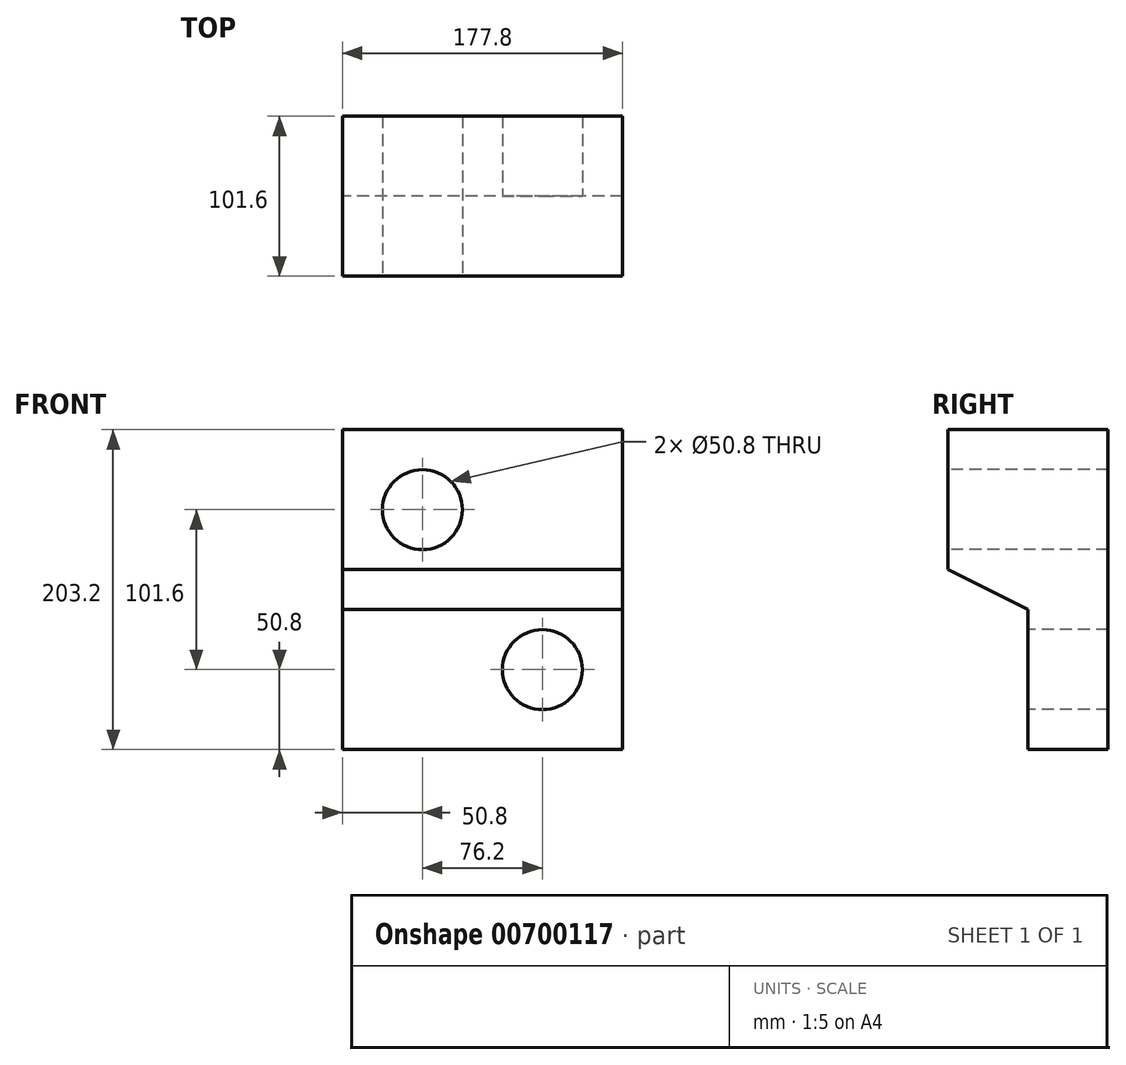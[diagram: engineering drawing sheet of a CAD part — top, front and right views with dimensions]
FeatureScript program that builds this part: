
annotation { "Feature Type Name" : "Feature", "Feature Type Description" : "" }
export const myFeature = defineFeature(function(context is Context, id is Id, definition is map)
    precondition{}
    {
        {
            var Q0;
            Q0=qCreatedBy(makeId("Right.planeOp"),FACE);
            var sketch = newSketch(context, id + "F0", { "sketchPlane" : qUnion([Q0])});
            skLineSegment(sketch, "E0", {"start": v(0, -88.9) * mm, "end": v(0, 0) * mm});
            skLineSegment(sketch, "E1", {"start": v(0, -88.9) * mm, "end": v(50.8, -88.9) * mm});
            skLineSegment(sketch, "E2", {"start": v(50.8, -88.9) * mm, "end": v(50.8, 114.3) * mm});
            skLineSegment(sketch, "E3", {"start": v(50.8, 114.3) * mm, "end": v(-50.8, 114.3) * mm});
            skLineSegment(sketch, "E4", {"start": v(-50.8, 114.3) * mm, "end": v(-50.8, 25.4) * mm});
            skLineSegment(sketch, "E5", {"start": v(-50.8, 25.4) * mm, "end": v(0, 0) * mm});
            skSolve(sketch);
        }
        {
            var Q0;
            Q0 = qSketchRegion(id + "F0", true);
            extrude(context, id + "F1", {"entities" : qUnion([Q0]), "depth" : 177.8 * mm, "offsetDistance" : 25.4 * mm});
        }
        {
            var Q0;
            Q0=qCreatedBy(makeId("Front.planeOp"),FACE);
            var sketch = newSketch(context, id + "F2", { "sketchPlane" : qUnion([Q0])});
            skCircle(sketch, "E6", {"center": v(50.8, 63.5) * mm, "radius": 25.4 * mm});
            skCircle(sketch, "E7", {"center": v(127, -38.1) * mm, "radius": 25.4 * mm});
            skSolve(sketch);
        }
        {
            var Q0;
            Q0 = qSketchRegion(id + "F2", true);
            extrude(context, id + "F3", {"entities" : qUnion([Q0]), "operationType" : NewBodyOperationType.REMOVE, "oppositeDirection" : true, "depth" : 136.4 * mm, "offsetDistance" : 25.4 * mm});
        }
        {
            var Q0;
            Q0=makeQuery(id+"F1.opExtrude","SWEPT_FACE",FACE,{"disambiguationData":[OSD([sQuery(id+"F0.wireOp",EDGE,"E2")])]});
            var sketch = newSketch(context, id + "F4", { "sketchPlane" : qUnion([Q0])});
            skCircle(sketch, "E8", {"center": v(-50.8, 63.5) * mm, "radius": 25.4 * mm});
            skSolve(sketch);
        }
        {
            var Q0;
            Q0 = qSketchRegion(id + "F4", true);
            extrude(context, id + "F5", {"entities" : qUnion([Q0]), "operationType" : NewBodyOperationType.REMOVE, "oppositeDirection" : true, "depth" : 138.68 * mm, "offsetDistance" : 25.4 * mm});
        }
    });
